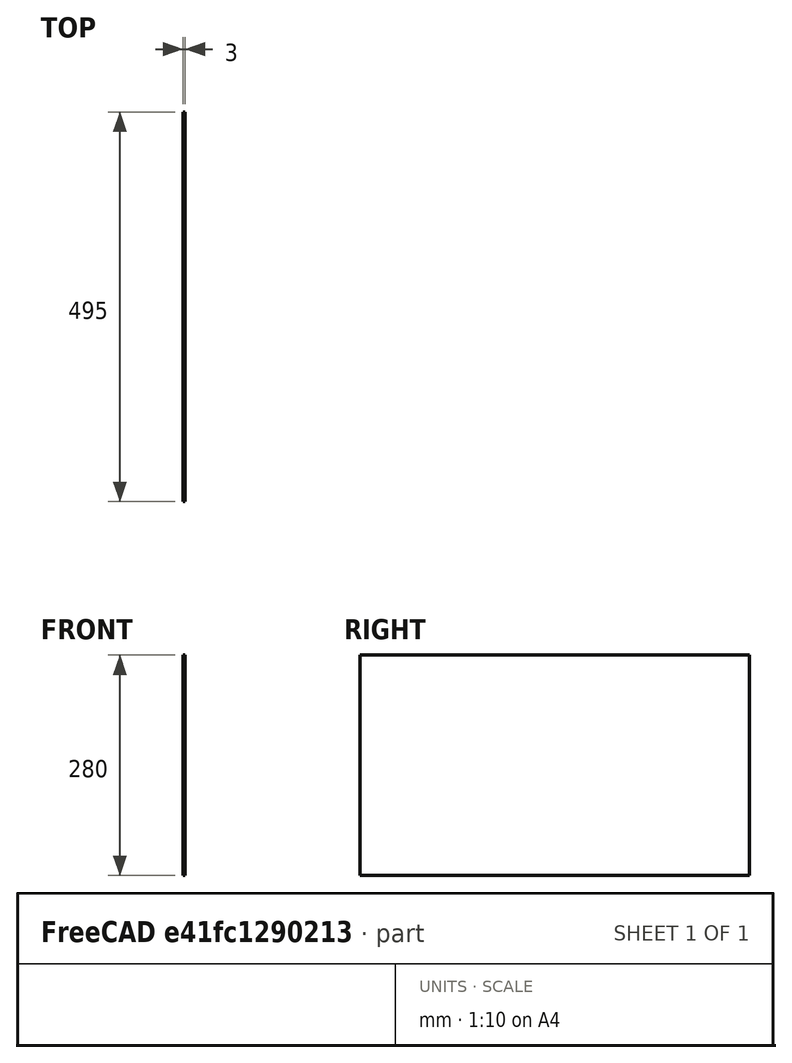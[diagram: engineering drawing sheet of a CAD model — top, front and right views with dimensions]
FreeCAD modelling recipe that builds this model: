
FCSTD DOCUMENT  (FreeCAD 0.19R24291 (Git))
Label: 8000_Back_wall
License: All rights reserved
LicenseURL: http://en.wikipedia.org/wiki/All_rights_reserved
objects: Sketcher::SketchObject×1, PartDesign::Pad×1, PartDesign::Body×1
note: 4 computed .brp shape members not serialized (recipe doc carries the construction recipe); baked Part::Feature solids carry a one-line shape summary decoded from their .brp

FEATURE [Sketcher::SketchObject] Sketch
  FullyConstrained = true
  MapMode = 5
  Placement = pos=(0,0,0) rot=(0.57735,0.57735,0.57735;2.0944rad)
  Support = -> [YZ_Plane]
  sketch-geometry (4):
    g0: LineSegment StartX=0 StartY=280 StartZ=0 EndX=495 EndY=280 EndZ=0
    g1: LineSegment StartX=495 StartY=280 StartZ=0 EndX=495 EndY=0 EndZ=0
    g2: LineSegment StartX=495 StartY=0 StartZ=0 EndX=0 EndY=0 EndZ=0
    g3: LineSegment StartX=0 StartY=0 StartZ=0 EndX=0 EndY=280 EndZ=0
  constraints (11):
    c: Coincident(g0,g1)
    c: Coincident(g1,g2)
    c: Coincident(g2,g3)
    c: Coincident(g3,g0)
    c: Horizontal(g0)
    c: Horizontal(g2)
    c: Vertical(g1)
    c: Vertical(g3)
    c: DistanceX(g0,g0) = 495
    c: DistanceY(g3,g3) = 280
    c: Coincident(g2,g-1)
FEATURE [PartDesign::Pad] Pad
  Direction = (1,1,1)
  Length = 3
  Length2 = 100
  Placement = pos=(0,0,0) rot=(0.57735,0.57735,0.57735;2.0944rad)
  Profile = -> Sketch
  Type = 0
FEATURE [PartDesign::Body] Body
  Group = -> [Sketch,Pad]
  Origin = -> Origin
  Tip = -> Pad
